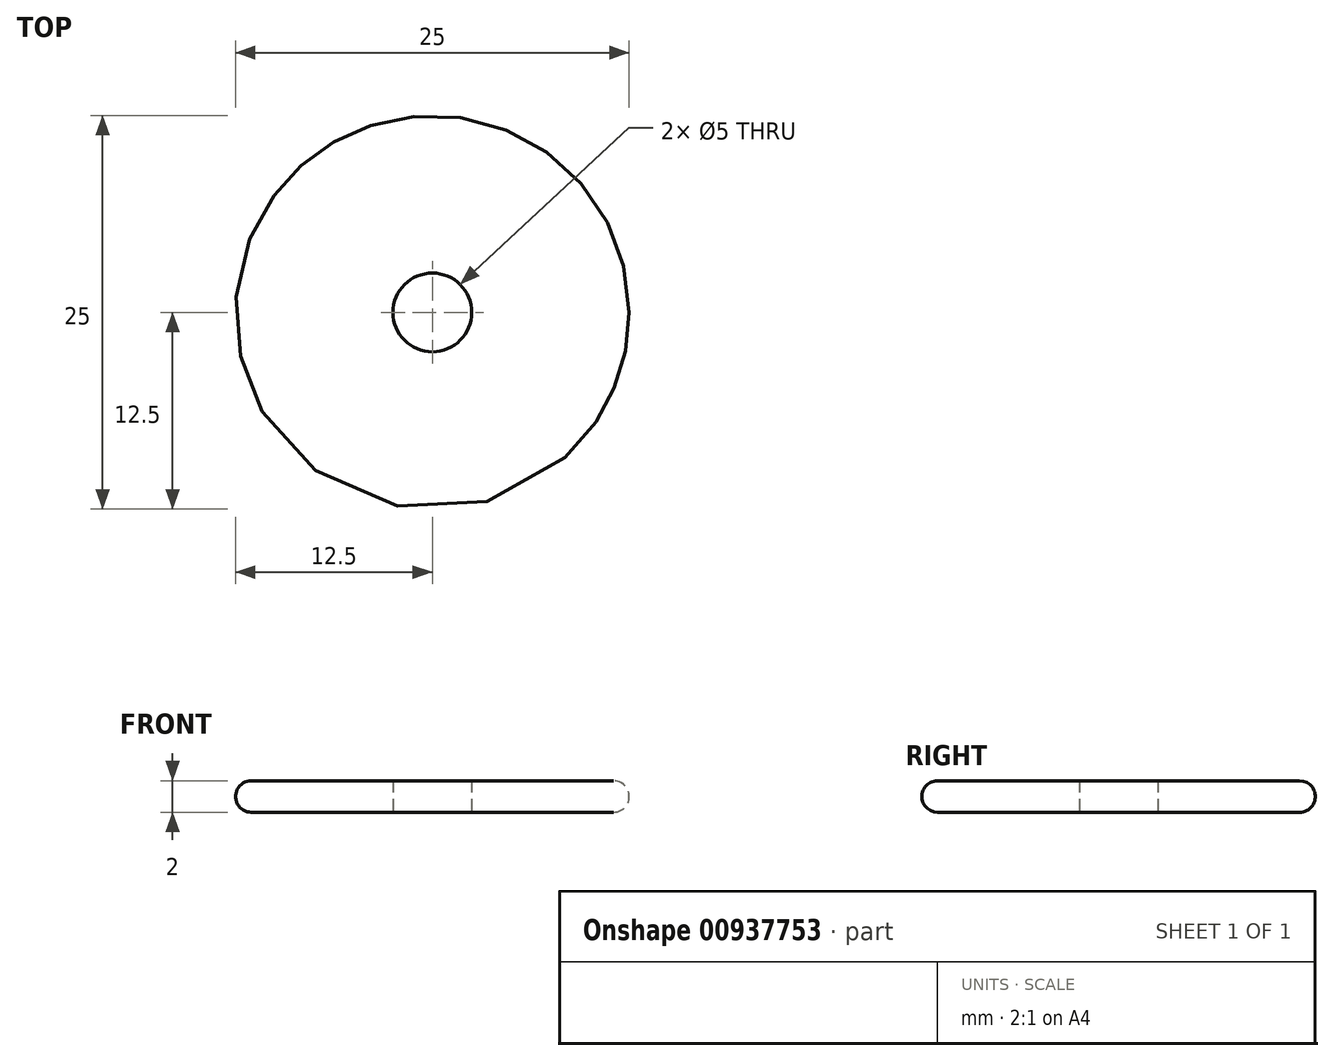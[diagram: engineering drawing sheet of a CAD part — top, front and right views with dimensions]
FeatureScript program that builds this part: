
annotation { "Feature Type Name" : "Feature", "Feature Type Description" : "" }
export const myFeature = defineFeature(function(context is Context, id is Id, definition is map)
    precondition{}
    {
        {
            var Q0;
            Q0=qCreatedBy(makeId("Top.planeOp"),FACE);
            var sketch = newSketch(context, id + "F0", { "sketchPlane" : qUnion([Q0])});
            skCircle(sketch, "E0", {"center": v(0, 0) * mm, "radius": 12.5 * mm});
            skCircle(sketch, "E1", {"center": v(0, 0) * mm, "radius": 2.5 * mm});
            skSolve(sketch);
        }
        {
            var Q0;
            Q0=qSketchRegion(id+"F0",true);
            extrude(context, id + "F1", {"entities" : qUnion([Q0]), "depth" : 2 * mm, "offsetDistance" : 25 * mm});
        }
        {
            var Q0;
            Q0=makeQuery(id+"F1.opExtrude","CAP_EDGE",EDGE,{"disambiguationData":[OSD([sQuery(id+"F0.wireOp",EDGE,"E0")])],"isStart":false});
            fillet(context, id + "F2", {"entities" : qUnion([Q0]), "radius" : 1 * mm, "tangentPropagation" : true, "allowEdgeOverflow" : false});
        }
        {
            var Q0;
            Q0=makeQuery(id+"F1.opExtrude","CAP_EDGE",EDGE,{"disambiguationData":[OSD([sQuery(id+"F0.wireOp",EDGE,"E0")])],"isStart":true});
            fillet(context, id + "F3", {"entities" : qUnion([Q0]), "radius" : 1 * mm, "tangentPropagation" : true, "allowEdgeOverflow" : false});
        }
    });
